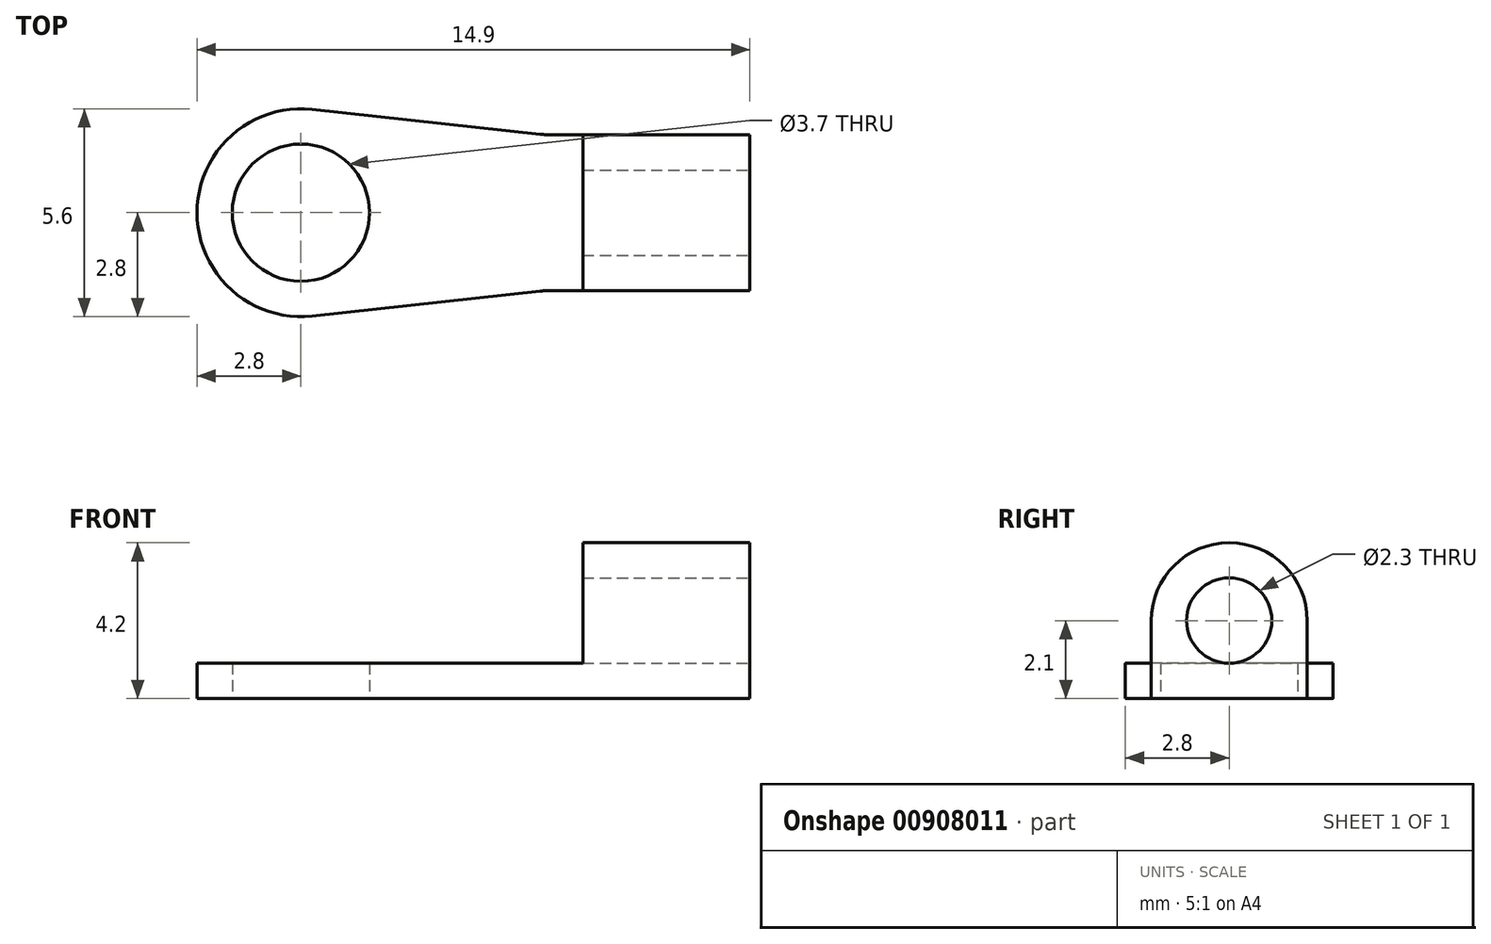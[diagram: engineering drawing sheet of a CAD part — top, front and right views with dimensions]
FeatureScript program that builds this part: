
annotation { "Feature Type Name" : "Feature", "Feature Type Description" : "" }
export const myFeature = defineFeature(function(context is Context, id is Id, definition is map)
    precondition{}
    {
        {
            var Q0;
            Q0=qCreatedBy(makeId("Top.planeOp"),FACE);
            var sketch = newSketch(context, id + "F0", { "sketchPlane" : qUnion([Q0])});
            skLineSegment(sketch, "E0.left", {"start": v(0, 2.8) * mm, "end": v(0, 2.8) * mm});
            skLineSegment(sketch, "E0.right", {"start": v(14.9, 0.7) * mm, "end": v(14.9, 4.9) * mm});
            skPoint(sketch, "E1.visualSharp", {"position": v(0, 5.6) * mm});
            skArc(sketch, "E1.filletArc", {"start": v(2.8, 5.6) * mm, "mid": v(0.82, 4.78) * mm, "end": v(0, 2.8) * mm});
            skPoint(sketch, "E2.visualSharp", {"position": v(0, 0) * mm});
            skArc(sketch, "E2.filletArc", {"start": v(0, 2.8) * mm, "mid": v(0.82, 0.82) * mm, "end": v(2.8, 0) * mm});
            skLineSegment(sketch, "E3.bottom", {"start": v(14.9, 0.7) * mm, "end": v(9.55, 0.7) * mm});
            skLineSegment(sketch, "E3.top", {"start": v(14.9, 4.9) * mm, "end": v(10.4, 4.9) * mm});
            skPoint(sketch, "E3.middle", {"position": v(14.9, 2.8) * mm});
            skLineSegment(sketch, "E4", {"start": v(10.4, 4.9) * mm, "end": v(9.55, 4.9) * mm});
            skArc(sketch, "E5", {"start": v(3.1, 5.58) * mm, "mid": v(0, 2.8) * mm, "end": v(3.1, 0.02) * mm});
            skCircle(sketch, "E6", {"center": v(2.8, 2.8) * mm, "radius": 1.85 * mm});
            skLineSegment(sketch, "E7", {"start": v(9.25, 4.92) * mm, "end": v(3.1, 5.58) * mm});
            skLineSegment(sketch, "E8", {"start": v(9.25, 0.68) * mm, "end": v(3.1, 0.02) * mm});
            skPoint(sketch, "E9.visualSharp", {"position": v(9.4, 4.9) * mm});
            skArc(sketch, "E9.filletArc", {"start": v(9.25, 4.92) * mm, "mid": v(9.4, 4.9) * mm, "end": v(9.55, 4.9) * mm});
            skPoint(sketch, "E10.visualSharp", {"position": v(9.4, 0.7) * mm});
            skArc(sketch, "E10.filletArc", {"start": v(9.55, 0.7) * mm, "mid": v(9.4, 0.7) * mm, "end": v(9.25, 0.68) * mm});
            skPoint(sketch, "E11.orphan", {"position": v(19.4, 4.9) * mm});
            skPoint(sketch, "E12.orphan", {"position": v(19.4, 0.7) * mm});
            skPoint(sketch, "E0.top.end.orphan", {"position": v(14.9, 5.6) * mm});
            skPoint(sketch, "E0.bottom.end.orphan", {"position": v(14.9, 0) * mm});
            skPoint(sketch, "E3.right.start.orphan", {"position": v(10.4, 0.7) * mm});
            skSolve(sketch);
        }
        {
            var Q0;
            Q0=makeQuery(id+"F0.imprint","IMPRINT",FACE,{"disambiguationData":[TD([[makeQuery(id+"F0.imprint","IMPRINT",EDGE,{"derivedFrom":sQuery(id+"F0.wireOp",EDGE,"E0.right")}),1.0]])]});
            extrude(context, id + "F1", {"entities" : qUnion([Q0]), "depth" : 0.95 * mm, "offsetDistance" : 25 * mm});
        }
        {
            var Q0;
            Q0=makeQuery(id+"F1.opExtrude","CAP_FACE",FACE,{"disambiguationData":[OSD([sQuery(id+"F0.wireOp",EDGE,"E0.right"),sQuery(id+"F0.wireOp",EDGE,"E3.bottom"),sQuery(id+"F0.wireOp",EDGE,"E3.top"),sQuery(id+"F0.wireOp",EDGE,"E4"),sQuery(id+"F0.wireOp",EDGE,"E5"),sQuery(id+"F0.wireOp",EDGE,"E6"),sQuery(id+"F0.wireOp",EDGE,"E7"),sQuery(id+"F0.wireOp",EDGE,"E8"),sQuery(id+"F0.wireOp",EDGE,"E9.filletArc"),sQuery(id+"F0.wireOp",EDGE,"E10.filletArc")])],"isStart":false});
            var sketch = newSketch(context, id + "F2", { "sketchPlane" : qUnion([Q0])});
            skLineSegment(sketch, "E13.bottom", {"start": v(14.9, 4.9) * mm, "end": v(10.4, 4.9) * mm});
            skLineSegment(sketch, "E13.top", {"start": v(14.9, 0.7) * mm, "end": v(10.4, 0.7) * mm});
            skLineSegment(sketch, "E13.left", {"start": v(14.9, 4.9) * mm, "end": v(14.9, 0.7) * mm});
            skLineSegment(sketch, "E13.right", {"start": v(10.4, 4.9) * mm, "end": v(10.4, 0.7) * mm});
            skSolve(sketch);
        }
        {
            var Q0;
            Q0=makeQuery(id+"F2.imprint","IMPRINT",FACE,{"disambiguationData":[TD([[makeQuery(id+"F2.imprint","IMPRINT",EDGE,{"derivedFrom":sQuery(id+"F2.wireOp",EDGE,"E13.bottom")}),1.0]])]});
            extrude(context, id + "F3", {"entities" : qUnion([Q0]), "operationType" : NewBodyOperationType.ADD, "depth" : 3.25 * mm, "offsetDistance" : 25 * mm});
        }
        {
            var Q0;
            Q0=makeQuery(id+"F3.opExtrude","CAP_EDGE",EDGE,{"disambiguationData":[OSD([sQuery(id+"F2.wireOp",EDGE,"E13.bottom")])],"isStart":false});
            var Q1;
            Q1=makeQuery(id+"F3.opExtrude","CAP_EDGE",EDGE,{"disambiguationData":[OSD([sQuery(id+"F2.wireOp",EDGE,"E13.top")])],"isStart":false});
            fillet(context, id + "F4", {"entities" : qUnion([Q0, Q1]), "radius" : 2.1 * mm, "tangentPropagation" : true, "allowEdgeOverflow" : false});
        }
        {
            var Q0;
            Q0=makeQuery(id+"F3.boolean.opBoolean","MERGE",FACE,{"derivedFrom":[makeQuery(id+"F1.opExtrude","SWEPT_FACE",FACE,{"disambiguationData":[OSD([sQuery(id+"F0.wireOp",EDGE,"E0.right")])]}),makeQuery(id+"F3.opExtrude","SWEPT_FACE",FACE,{"disambiguationData":[OSD([sQuery(id+"F2.wireOp",EDGE,"E13.left")])]})]});
            var sketch = newSketch(context, id + "F5", { "sketchPlane" : qUnion([Q0])});
            skCircle(sketch, "E14", {"center": v(2.8, 2.1) * mm, "radius": 1.15 * mm});
            skSolve(sketch);
        }
        {
            var Q0;
            Q0=makeQuery(id+"F5.imprint","IMPRINT",FACE,{"disambiguationData":[TD([[makeQuery(id+"F5.imprint","IMPRINT",EDGE,{"derivedFrom":sQuery(id+"F5.wireOp",EDGE,"E14")}),1.0]])]});
            extrude(context, id + "F6", {"entities" : qUnion([Q0]), "operationType" : NewBodyOperationType.REMOVE, "oppositeDirection" : true, "depth" : 25 * mm, "offsetDistance" : 25 * mm});
        }
    });
